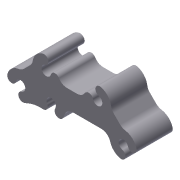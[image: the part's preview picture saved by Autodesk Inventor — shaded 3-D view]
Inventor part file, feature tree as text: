
AUTODESK INVENTOR PART (.ipt)
format: ipt  version: 2013 (Build 170138000, 138)  size: 159,232 bytes
history: native  units: in
note: dims shown in document units (in); Inventor stores cm internally (conversion verified against a paired STEP export)
features: extrude x1, sketch x1
ambient origin geometry x8: Origin, YZ Plane, XZ Plane, XY Plane, X Axis, Y Axis, Z Axis, Center Point
bodies: Solid1 (feature_tree)
feature tree (2):
  extrude  "Extrusion1"  [1 undecoded]
  sketch  "Sketch1"  dims[d0=0.995in d1=0.0in]
note: 1 required parameter value undecoded (feature->parameter linkage not recoverable at this tier; creation-order binding heuristic only, values carry confidence <= 0.55)
